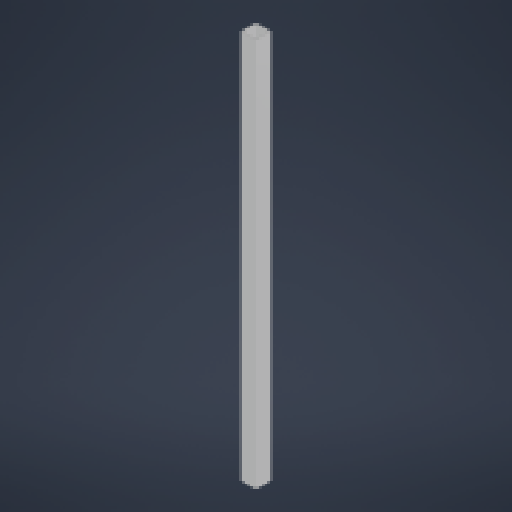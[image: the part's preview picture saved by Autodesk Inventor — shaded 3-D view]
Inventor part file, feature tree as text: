
AUTODESK INVENTOR PART (.ipt)
format: ipt  version: 2024 (Build 280153000, 153)  size: 129,536 bytes
history: native  units: mm
features: extrude x1
ambient origin geometry x8: Origin, YZ Plane, XZ Plane, XY Plane, X Axis, Y Axis, Z Axis, Center Point
bodies: Solid1 (feature_tree)
feature tree (1):
  extrude  "Extrusion1"  Depth=25.4mm
